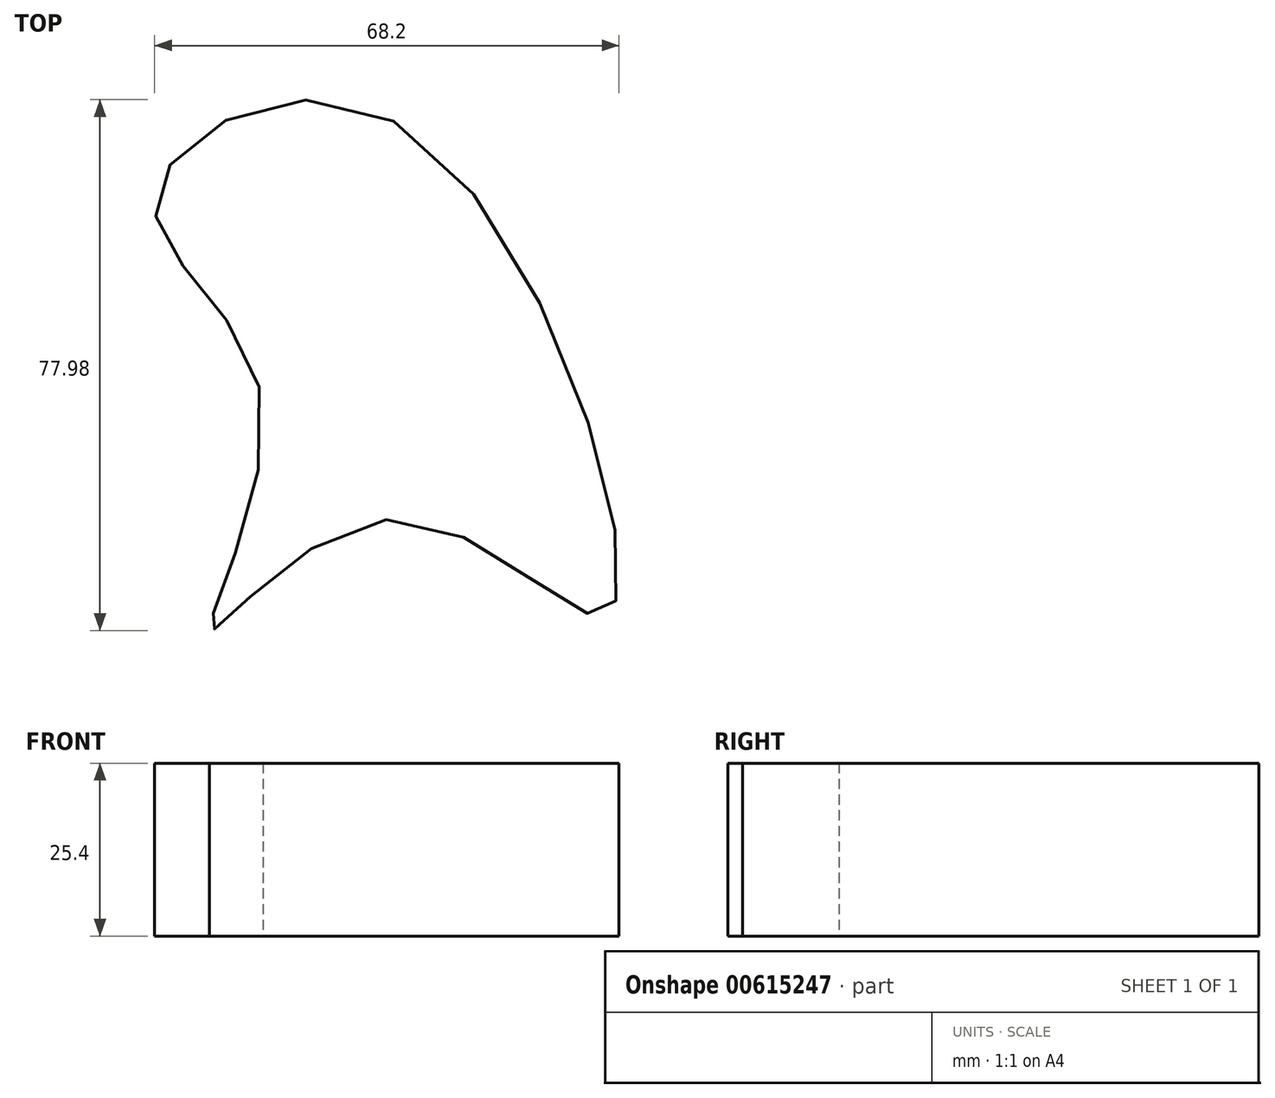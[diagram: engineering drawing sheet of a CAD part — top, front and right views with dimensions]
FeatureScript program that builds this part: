
annotation { "Feature Type Name" : "Feature", "Feature Type Description" : "" }
export const myFeature = defineFeature(function(context is Context, id is Id, definition is map)
    precondition{}
    {
        {
            var Q0;
            Q0=qCreatedBy(makeId("Top.planeOp"),FACE);
            var sketch = newSketch(context, id + "F0", { "sketchPlane" : qUnion([Q0])});
            skFitSpline(sketch, "E0", {"points": [v(0, 40.57) * mm, v(-35.01, 29.09) * mm, v(-19.45, 0) * mm, v(-26.86, -34.27) * mm, v(0, -17.97) * mm, v(31.68, -31.68) * mm, v(0, 40.57) * mm]});
            skSolve(sketch);
        }
        {
            var Q0;
            Q0=makeQuery(id+"F0.imprint","IMPRINT",FACE,{"disambiguationData":[TD([[makeQuery(id+"F0.imprint","IMPRINT",EDGE,{"derivedFrom":sQuery(id+"F0.wireOp",EDGE,"E0")}),1.0]])]});
            extrude(context, id + "F1", {"entities" : qUnion([Q0]), "depth" : 25.4 * mm, "offsetDistance" : 25.4 * mm});
        }
    });
